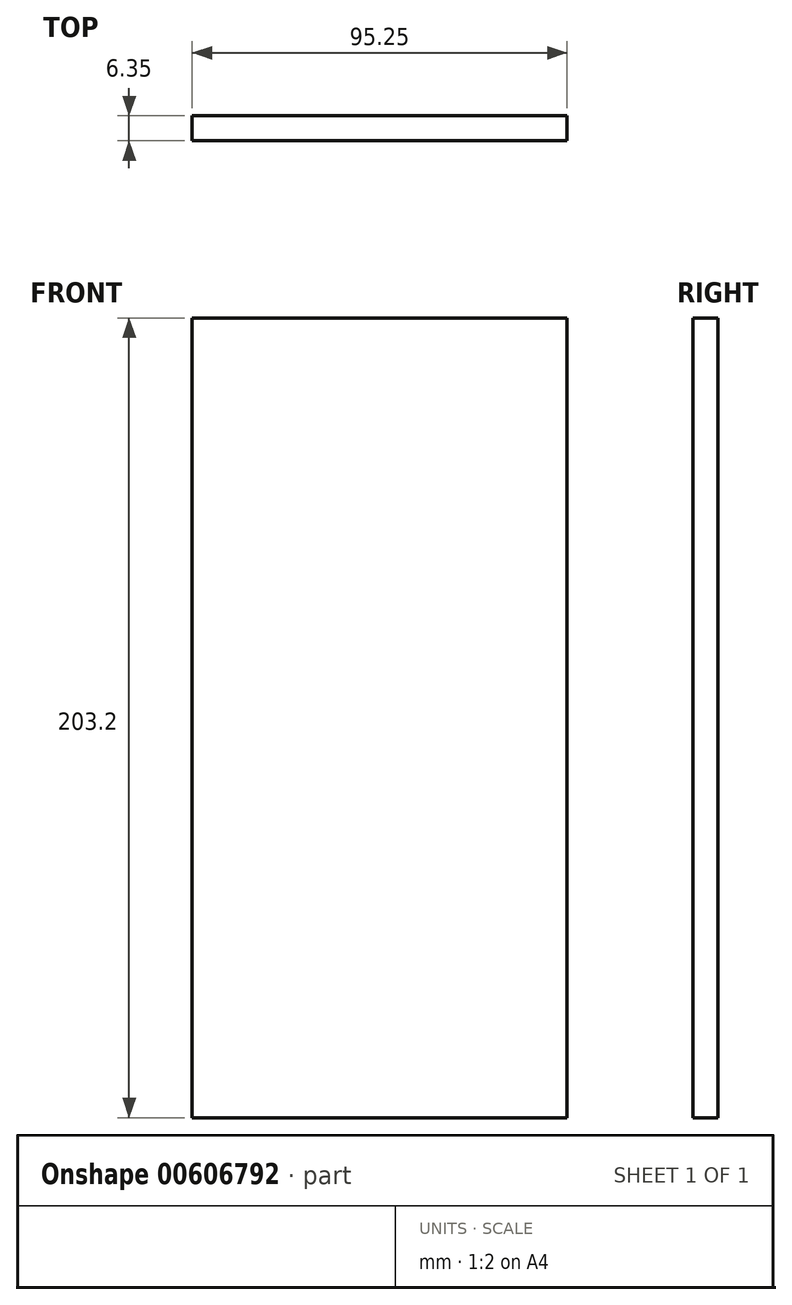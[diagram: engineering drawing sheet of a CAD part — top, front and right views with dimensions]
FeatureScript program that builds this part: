
annotation { "Feature Type Name" : "Feature", "Feature Type Description" : "" }
export const myFeature = defineFeature(function(context is Context, id is Id, definition is map)
    precondition{}
    {
        {
            var Q0;
            Q0=qCreatedBy(makeId("Front.planeOp"),FACE);
            var sketch = newSketch(context, id + "F0", { "sketchPlane" : qUnion([Q0])});
            skLineSegment(sketch, "E0.bottom", {"start": v(-45.03, 168.09) * mm, "end": v(50.22, 168.09) * mm});
            skLineSegment(sketch, "E0.top", {"start": v(-45.03, -35.11) * mm, "end": v(50.22, -35.11) * mm});
            skLineSegment(sketch, "E0.left", {"start": v(-45.03, 168.09) * mm, "end": v(-45.03, -35.11) * mm});
            skLineSegment(sketch, "E0.right", {"start": v(50.22, 168.09) * mm, "end": v(50.22, -35.11) * mm});
            skSolve(sketch);
        }
        {
            var Q0;
            Q0 = qSketchRegion(id + "F0", true);
            extrude(context, id + "F1", {"entities" : qUnion([Q0]), "depth" : 6.35 * mm, "offsetDistance" : 25.4 * mm});
        }
    });
